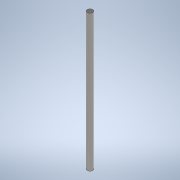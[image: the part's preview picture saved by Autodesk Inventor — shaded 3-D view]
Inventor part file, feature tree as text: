
AUTODESK INVENTOR PART (.ipt)
format: ipt  version: 2021 (Build 250183000, 183)  size: 90,112 bytes
history: native  units: mm
features: other x1, extrude x1, sketch x1
ambient origin geometry x8: Origin, YZ Plane, XZ Plane, XY Plane, X Axis, Y Axis, Z Axis, Center Point
bodies: Body1 (feature_tree)
feature tree (3):
  other  "實體1"
  extrude  "擠出1"  Depth=8.0mm
  sketch  "草圖1"
